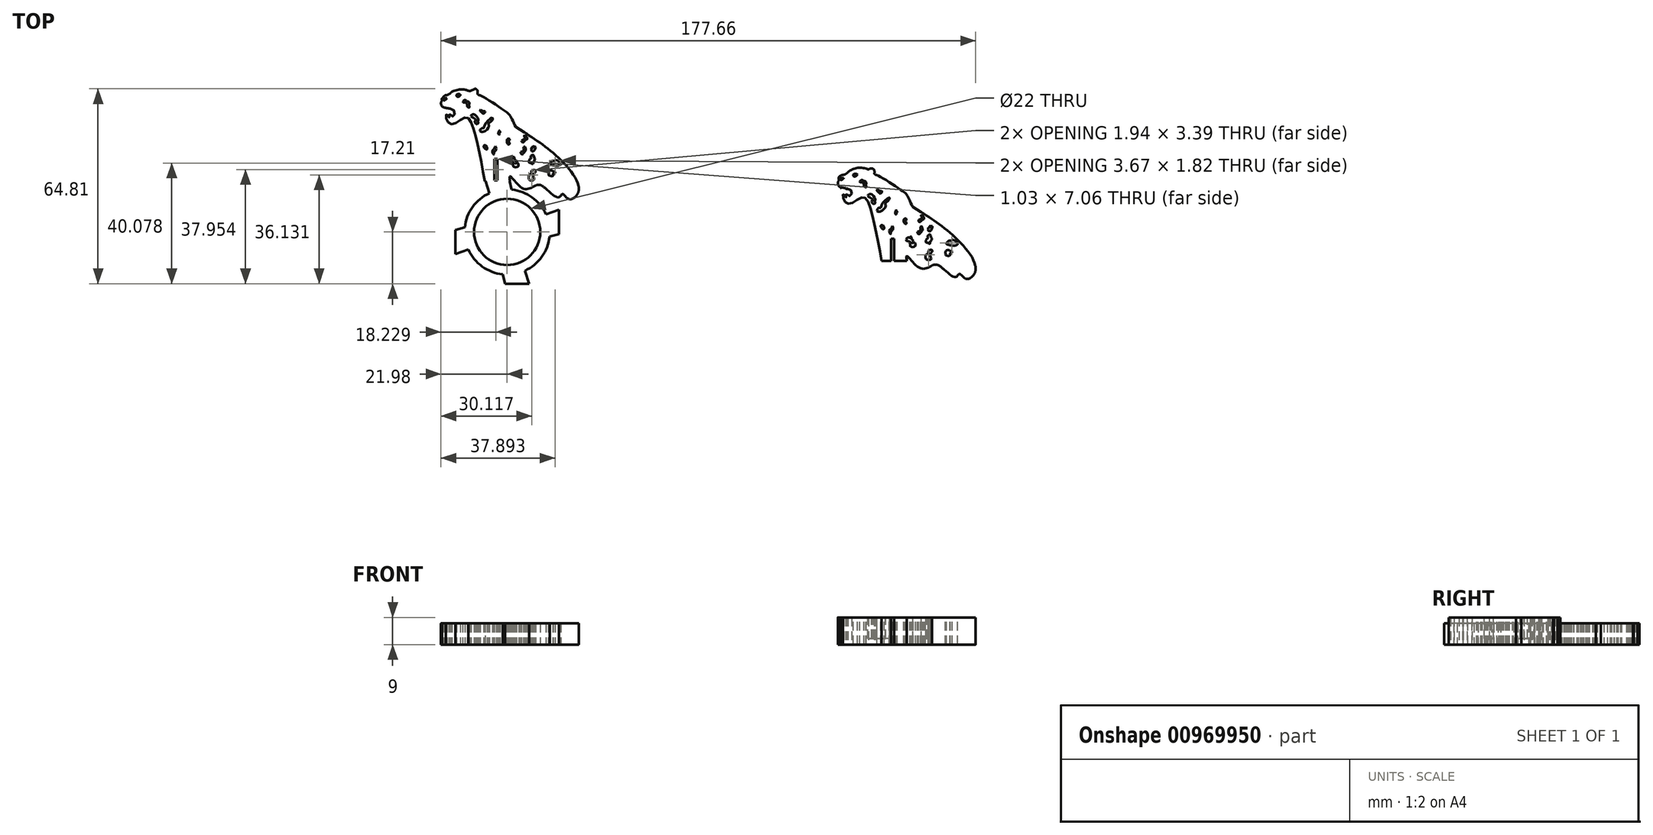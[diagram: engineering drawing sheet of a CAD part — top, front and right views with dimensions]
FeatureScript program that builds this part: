
annotation { "Feature Type Name" : "Feature", "Feature Type Description" : "" }
export const myFeature = defineFeature(function(context is Context, id is Id, definition is map)
    precondition{}
    {
        {
            var Q0;
            Q0=qCreatedBy(makeId("Top.planeOp"),FACE);
            var sketch = newSketch(context, id + "F0", { "sketchPlane" : qUnion([Q0])});
            skCircle(sketch, "E0", {"center": v(0, 0) * mm, "radius": 11 * mm});
            skCircle(sketch, "E1", {"center": v(0, 0) * mm, "radius": 46.71 * mm});
            skArc(sketch, "E2", {"start": v(-5.89, 12.9) * mm, "mid": v(2.27, -14) * mm, "end": v(1.52, 14.1) * mm});
            skLineSegment(sketch, "E3", {"start": v(137.48, 6.65) * mm, "end": v(134.7, 8.38) * mm});
            skFitSpline(sketch, "E4", {"points": [v(134.7, 8.38) * mm, v(132.83, 12.2) * mm, v(131.06, 13.79) * mm, v(122.58, 19) * mm, v(122.4, 19) * mm, v(121.92, 21.06) * mm, v(119.69, 20.4) * mm, v(117.45, 20.87) * mm, v(110.56, 18.26) * mm, v(110.28, 15.18) * mm, v(114.28, 13.79) * mm, v(113.82, 11.92) * mm, v(112.6, 12.67) * mm, v(112.6, 11.55) * mm, v(111.77, 12.58) * mm, v(111.77, 10.8) * mm, v(114, 9.4) * mm, v(118.2, 11.55) * mm, v(121.09, 6.52) * mm, v(124.44, -9.6) * mm], "startDerivative": vector(-33.74, 75.54) * mm, "endDerivative": vector(26.94, -147.55) * mm});
            skLineSegment(sketch, "E5", {"start": v(124.44, -9.6) * mm, "end": v(127.6, -9.6) * mm});
            skLineSegment(sketch, "E6", {"start": v(127.6, -9.6) * mm, "end": v(127.6, -2.24) * mm});
            skLineSegment(sketch, "E7", {"start": v(127.6, -2.24) * mm, "end": v(128.63, -2.24) * mm});
            skLineSegment(sketch, "E8", {"start": v(128.63, -2.24) * mm, "end": v(128.63, -9.6) * mm});
            skLineSegment(sketch, "E9", {"start": v(128.63, -9.6) * mm, "end": v(132.83, -9.6) * mm});
            skFitSpline(sketch, "E10", {"points": [v(132.83, -9.6) * mm, v(132.83, -8.02) * mm, v(136.93, -11.93) * mm, v(141.22, -11.13) * mm], "startDerivative": vector(-1.77, 10.95) * mm, "endDerivative": vector(11.78, 6.45) * mm});
            skFitSpline(sketch, "E11", {"points": [v(141.22, -11.13) * mm, v(143.33, -11.13) * mm, v(148.92, -15.03) * mm, v(150.32, -13.91) * mm, v(152.37, -15.59) * mm, v(155.63, -12.8) * mm, v(148.64, -1.6) * mm, v(137.48, 6.65) * mm], "startDerivative": vector(20.39, 8.24) * mm, "endDerivative": vector(-48.7, 31.34) * mm});
            skFitSpline(sketch, "E12", {"points": [v(155.57, -11.13) * mm, v(162.62, -16.87) * mm], "startDerivative": vector(5.16, -7.62) * mm, "endDerivative": vector(8.98, -3.93) * mm});
            skLineSegment(sketch, "E13", {"start": v(162.62, -16.87) * mm, "end": v(154.78, -14.58) * mm});
            skFitSpline(sketch, "E14", {"points": [v(115.12, 19.2) * mm, v(116.34, 19.1) * mm, v(115.28, 18.46) * mm, v(115.12, 19.2) * mm]});
            skFitSpline(sketch, "E15", {"points": [v(122.82, 7) * mm, v(123.58, 8.07) * mm, v(124.09, 8) * mm, v(124.53, 9.2) * mm, v(126.99, 11.42) * mm, v(126.74, 10.47) * mm, v(125.66, 9.52) * mm, v(125.79, 8.7) * mm, v(124.34, 6.94) * mm, v(122.82, 7) * mm]});
            skFitSpline(sketch, "E16", {"points": [v(124.09, 2.04) * mm, v(124.96, 2.07) * mm, v(125.06, 0.9) * mm, v(124.09, 2.04) * mm]});
            skFitSpline(sketch, "E17", {"points": [v(119.85, 12.04) * mm, v(121.09, 11.13) * mm, v(121.46, 10.56) * mm, v(121.09, 10.24) * mm, v(121.71, 9.3) * mm, v(122.03, 9.55) * mm, v(122.34, 9.67) * mm, v(122.03, 10.43) * mm, v(122.31, 10.46) * mm, v(121.52, 12.17) * mm, v(120.39, 12.58) * mm, v(119.85, 12.04) * mm]});
            skFitSpline(sketch, "E18", {"points": [v(118.2, 16.4) * mm, v(117.64, 16.52) * mm, v(117.13, 16.68) * mm, v(117.96, 17.4) * mm, v(118.4, 16.8) * mm, v(118.84, 16.93) * mm, v(119.34, 15.99) * mm, v(119.15, 15.77) * mm, v(119.28, 15.35) * mm, v(119.28, 14.85) * mm, v(118.65, 15.17) * mm, v(118.55, 15.8) * mm, v(118.2, 16.4) * mm]});
            skFitSpline(sketch, "E19", {"points": [v(128.9, 6.1) * mm, v(128.97, 6.52) * mm, v(129.22, 7.21) * mm, v(129.44, 7.02) * mm, v(129.54, 6.52) * mm, v(129.25, 6.52) * mm, v(129.32, 5.92) * mm, v(128.9, 6.1) * mm]});
            skFitSpline(sketch, "E20", {"points": [v(132.28, 2.64) * mm, v(131.84, 3.27) * mm, v(131.87, 4.18) * mm, v(132.54, 4.47) * mm, v(132.66, 3.96) * mm, v(132.25, 3.74) * mm, v(132.22, 3.36) * mm, v(132.6, 3.2) * mm, v(132.6, 2.73) * mm, v(132.28, 2.64) * mm]});
            skFitSpline(sketch, "E21", {"points": [v(139.04, -8.52) * mm, v(139.23, -7.59) * mm, v(139.98, -7.06) * mm, v(139.9, -6.38) * mm, v(140.92, -5.9) * mm, v(141.3, -6.42) * mm, v(140.5, -7.4) * mm, v(140.73, -8.3) * mm, v(140.77, -9.16) * mm, v(139.87, -9.31) * mm, v(139.23, -9.16) * mm, v(139.04, -8.52) * mm]});
            skFitSpline(sketch, "E22", {"points": [v(141.25, 1.87) * mm, v(140.9, 1.87) * mm, v(140.59, 1.95) * mm, v(140.3, 1.85) * mm, v(140.4, 1.45) * mm, v(139.84, 1.37) * mm, v(139.98, 0.94) * mm, v(139.84, 0.63) * mm, v(140.24, 0.28) * mm, v(140.64, 0.36) * mm, v(141.1, 1) * mm, v(141.25, 1.87) * mm]});
            skFitSpline(sketch, "E23", {"points": [v(132.57, -2.43) * mm, v(133.05, -3.06) * mm, v(133.83, -3.14) * mm, v(133.9, -3.46) * mm, v(133.78, -3.7) * mm, v(133.85, -4.22) * mm, v(133.9, -4.72) * mm, v(134.28, -4.9) * mm, v(134.53, -5.05) * mm, v(134.86, -4.92) * mm, v(135.44, -4.87) * mm, v(135.69, -4.42) * mm, v(135.49, -3.64) * mm, v(135.23, -3.39) * mm, v(134.88, -3.82) * mm, v(134.5, -3.54) * mm, v(134.93, -3.01) * mm, v(134.36, -2.36) * mm, v(134.23, -1.53) * mm, v(133.95, -1.56) * mm, v(133.83, -2.03) * mm, v(133.5, -1.78) * mm, v(132.95, -2.06) * mm, v(132.57, -2.43) * mm]});
            skFitSpline(sketch, "E24", {"points": [v(136.67, 3.8) * mm, v(137.04, 3.27) * mm, v(137.32, 3.4) * mm, v(137.4, 3.67) * mm, v(137.67, 3.67) * mm, v(137.75, 4.2) * mm, v(138.35, 4.2) * mm, v(138.47, 4.87) * mm, v(137.72, 5.48) * mm, v(137.42, 5.37) * mm, v(137.85, 5.02) * mm, v(137.8, 4.55) * mm, v(137.3, 4.2) * mm, v(136.67, 3.8) * mm]});
            skFitSpline(sketch, "E25", {"points": [v(136.31, 0) * mm, v(136.67, -0.68) * mm, v(137.14, -0.58) * mm, v(137.24, -0.3) * mm, v(137.5, -0.25) * mm, v(137.57, 0) * mm, v(138.07, 0.73) * mm, v(137.92, 1.26) * mm, v(137.67, 1.87) * mm, v(137.32, 1.45) * mm, v(137.37, 1) * mm, v(137.1, 0.35) * mm, v(136.31, 0) * mm]});
            skFitSpline(sketch, "E26", {"points": [v(127.98, 1.95) * mm, v(127.53, 1) * mm, v(126.97, 0.5) * mm, v(127.35, -0.73) * mm, v(127.53, 0) * mm, v(127.88, 0.43) * mm, v(128.2, 1) * mm, v(127.98, 1.95) * mm]});
            skFitSpline(sketch, "E27", {"points": [v(146.83, -6.06) * mm, v(147.12, -6.36) * mm, v(147.62, -6.41) * mm, v(147.86, -6.78) * mm, v(147.22, -7.05) * mm, v(147.07, -7.24) * mm, v(147.22, -7.62) * mm, v(146.8, -8) * mm, v(146.08, -7.86) * mm, v(145.61, -7.54) * mm, v(145.68, -7.25) * mm, v(145.56, -6.8) * mm, v(145.75, -6.34) * mm, v(146.12, -6.08) * mm, v(146.83, -6.06) * mm]});
            skFitSpline(sketch, "E28", {"points": [v(147.4, -2.85) * mm, v(146.69, -2.93) * mm, v(146.4, -3.29) * mm, v(145.94, -3.84) * mm, v(146.53, -4.27) * mm, v(147.45, -4.44) * mm, v(148.53, -4.57) * mm, v(149.21, -4.38) * mm, v(149.68, -4.1) * mm, v(149.44, -3.47) * mm, v(148.21, -2.64) * mm, v(147.4, -2.85) * mm]});
            skFitSpline(sketch, "E29", {"points": [v(140.12, -3.88) * mm, v(140.4, -3.92) * mm, v(140.59, -3.5) * mm, v(140.4, -3.34) * mm, v(140.7, -3.2) * mm, v(140.9, -2.87) * mm, v(141.1, -2.14) * mm, v(140.9, -1.86) * mm, v(140.77, -1.46) * mm, v(140.59, -0.92) * mm, v(140.06, -0.93) * mm, v(139.7, -1.67) * mm, v(139.83, -2.06) * mm, v(139.48, -2.26) * mm, v(139.14, -2.9) * mm, v(139.13, -3.44) * mm, v(139.47, -3.52) * mm, v(139.77, -3.64) * mm, v(140.12, -3.88) * mm]});
            skFitSpline(sketch, "E30", {"points": [v(123.2, 14.07) * mm, v(123.7, 13.63) * mm, v(124.33, 13.63) * mm, v(124.6, 13.37) * mm, v(124.3, 13.1) * mm, v(124.01, 12.76) * mm, v(123.44, 13.22) * mm, v(123.06, 13.52) * mm, v(122.87, 13.96) * mm, v(123.2, 14.07) * mm]});
            skLineSegment(sketch, "E31", {"start": v(0, 30.7) * mm, "end": v(131.87, 4.18) * mm, "construction": true});
            skLineSegment(sketch, "E32", {"start": v(-5.89, 12.9) * mm, "end": v(-7.34, 17.21) * mm});
            skLineSegment(sketch, "E33", {"start": v(-7.34, 17.21) * mm, "end": v(0.7, 17.21) * mm});
            skLineSegment(sketch, "E34", {"start": v(0.7, 17.21) * mm, "end": v(1.52, 14.1) * mm});
            skArc(sketch, "E35", {"start": v(110.28, 17.32) * mm, "mid": v(109.9, 16.25) * mm, "end": v(110.28, 15.18) * mm});
            skFitSpline(sketch, "E36.trimOffspring", {"points": [v(134.7, 8.38) * mm, v(132.83, 12.2) * mm, v(131.06, 13.79) * mm, v(122.58, 19) * mm, v(122.4, 19) * mm, v(121.92, 21.06) * mm, v(119.69, 20.4) * mm, v(117.45, 20.87) * mm, v(110.56, 18.26) * mm, v(110.28, 15.18) * mm, v(114.28, 13.79) * mm, v(113.82, 11.92) * mm, v(112.6, 12.67) * mm, v(112.6, 11.55) * mm, v(111.77, 12.58) * mm, v(111.77, 10.8) * mm, v(114, 9.4) * mm, v(118.2, 11.55) * mm, v(121.09, 6.52) * mm, v(124.44, -9.6) * mm], "startDerivative": vector(-33.74, 75.54) * mm, "endDerivative": vector(26.94, -147.55) * mm});
            skArc(sketch, "E37", {"start": v(110.16, 18.1) * mm, "mid": v(110.12, 17.7) * mm, "end": v(110.28, 17.32) * mm});
            skArc(sketch, "E38", {"start": v(111.62, 18.97) * mm, "mid": v(110.79, 18.7) * mm, "end": v(110.16, 18.1) * mm});
            skArc(sketch, "E39", {"start": v(111.62, 18.97) * mm, "mid": v(112.5, 19.26) * mm, "end": v(113.18, 19.88) * mm});
            skArc(sketch, "E40", {"start": v(120.05, 20.73) * mm, "mid": v(116.5, 21.31) * mm, "end": v(113.18, 19.88) * mm});
            skArc(sketch, "E41", {"start": v(122.03, 20.5) * mm, "mid": v(121.1, 21.12) * mm, "end": v(120.05, 20.73) * mm});
            skArc(sketch, "E42", {"start": v(122.03, 19.27) * mm, "mid": v(122.05, 19.88) * mm, "end": v(122.03, 20.5) * mm});
            skArc(sketch, "E43", {"start": v(122.4, 19) * mm, "mid": v(122.23, 19.17) * mm, "end": v(122.03, 19.27) * mm});
            skPoint(sketch, "E44.2.internal.orphan", {"position": v(110.56, 16.86) * mm});
            skArc(sketch, "E45", {"start": v(111.14, 17.89) * mm, "mid": v(110.75, 17.9) * mm, "end": v(110.72, 17.5) * mm});
            skArc(sketch, "E46", {"start": v(111.14, 17.89) * mm, "mid": v(111.5, 17.92) * mm, "end": v(111.87, 17.96) * mm});
            skArc(sketch, "E47", {"start": v(111.06, 17.26) * mm, "mid": v(111.52, 17.55) * mm, "end": v(111.87, 17.96) * mm});
            skArc(sketch, "E48", {"start": v(110.72, 17.5) * mm, "mid": v(110.82, 17.29) * mm, "end": v(111.06, 17.26) * mm});
            skArc(sketch, "E49", {"start": v(139.78, -11.91) * mm, "mid": v(139.1, -12.6) * mm, "end": v(139.36, -13.56) * mm});
            skArc(sketch, "E50", {"start": v(139.36, -13.56) * mm, "mid": v(139.6, -13.92) * mm, "end": v(140.05, -13.93) * mm});
            skArc(sketch, "E51", {"start": v(142.33, -12.8) * mm, "mid": v(141.14, -13.27) * mm, "end": v(140.05, -13.93) * mm});
            skArc(sketch, "E52", {"start": v(145.2, -12.55) * mm, "mid": v(143.74, -12.43) * mm, "end": v(142.33, -12.8) * mm});
            skLineSegment(sketch, "E53", {"start": v(139.78, -11.91) * mm, "end": v(141.22, -11.13) * mm});
            skArc(sketch, "E54", {"start": v(110.65, 14.56) * mm, "mid": v(110.69, 14.77) * mm, "end": v(110.67, 14.97) * mm});
            skArc(sketch, "E55", {"start": v(110.65, 14.56) * mm, "mid": v(110.88, 14.65) * mm, "end": v(111.03, 14.85) * mm});
            skArc(sketch, "E56", {"start": v(112.88, 14.15) * mm, "mid": v(112.93, 14.32) * mm, "end": v(112.87, 14.49) * mm});
            skArc(sketch, "E57", {"start": v(112.48, 14.56) * mm, "mid": v(112.64, 14.31) * mm, "end": v(112.88, 14.15) * mm});
            skSolve(sketch);
        }
        {
            var Q0;
            {var subQ5=sQuery(id+"F0.wireOp",EDGE,"E3");Q0=makeQuery(id+"F0.imprint","IMPRINT",FACE,{"disambiguationData":[TD([[makeQuery(id+"F0.imprint","IMPRINT",EDGE,{"derivedFrom":subQ5}),1.0]])]});}
            extrude(context, id + "F1", {"entities" : qUnion([Q0]), "depth" : 7 * mm, "offsetDistance" : 25 * mm});
        }
        {
            var Q0;
            Q0=qCreatedBy(makeId("Top.planeOp"),FACE);
            var sketch = newSketch(context, id + "F2", { "sketchPlane" : qUnion([Q0])});
            skCircle(sketch, "E58", {"center": v(0, 0) * mm, "radius": 11 * mm});
            skSolve(sketch);
        }
        {
            var Q0;
            Q0=makeQuery(id+"F1.opExtrude","SWEPT_BODY",BODY,{"disambiguationData":[OSD([sQuery(id+"F0.wireOp",EDGE,"E3"),sQuery(id+"F0.wireOp",EDGE,"E4"),sQuery(id+"F0.wireOp",EDGE,"E5"),sQuery(id+"F0.wireOp",EDGE,"E6"),sQuery(id+"F0.wireOp",EDGE,"E7"),sQuery(id+"F0.wireOp",EDGE,"E8"),sQuery(id+"F0.wireOp",EDGE,"E9"),sQuery(id+"F0.wireOp",EDGE,"E10"),sQuery(id+"F0.wireOp",EDGE,"E11"),sQuery(id+"F0.wireOp",EDGE,"E12"),sQuery(id+"F0.wireOp",EDGE,"E13"),sQuery(id+"F0.wireOp",EDGE,"E11"),sQuery(id+"F0.wireOp",EDGE,"E14"),sQuery(id+"F0.wireOp",EDGE,"E44"),sQuery(id+"F0.wireOp",EDGE,"E15"),sQuery(id+"F0.wireOp",EDGE,"E16"),sQuery(id+"F0.wireOp",EDGE,"E17"),sQuery(id+"F0.wireOp",EDGE,"E18"),sQuery(id+"F0.wireOp",EDGE,"E19"),sQuery(id+"F0.wireOp",EDGE,"E20"),sQuery(id+"F0.wireOp",EDGE,"E21"),sQuery(id+"F0.wireOp",EDGE,"E22"),sQuery(id+"F0.wireOp",EDGE,"E23"),sQuery(id+"F0.wireOp",EDGE,"E24"),sQuery(id+"F0.wireOp",EDGE,"E25"),sQuery(id+"F0.wireOp",EDGE,"E26"),sQuery(id+"F0.wireOp",EDGE,"E27"),sQuery(id+"F0.wireOp",EDGE,"E28"),sQuery(id+"F0.wireOp",EDGE,"E29"),sQuery(id+"F0.wireOp",EDGE,"E30")])]});
            var Q1;
            Q1=sQuery(id+"F0.wireOp",VERTEX,"E20.2.internal");
            var Q2;
            Q2=sQuery(id+"F0.wireOp",VERTEX,"E31.start");
            transform(context, id + "F3", {"entities" : qUnion([Q0]), "transformType" : TransformType.TRANSLATION_ENTITY, "oppositeDirectionEntity" : false, "transformLine" : qUnion([Q1, Q2]), "makeCopy" : false});
        }
        {
            var Q0;
            Q0=makeQuery(id+"F0.imprint","IMPRINT",FACE,{"disambiguationData":[TD([[makeQuery(id+"F0.imprint","IMPRINT",EDGE,{"derivedFrom":sQuery(id+"F0.wireOp",EDGE,"E0")}),-1.0]])]});
            var Q1;
            {var subQ0=sQuery(id+"F0.wireOp",EDGE,"E44");var subQ1=sQuery(id+"F0.wireOp",EDGE,"E4");var subQ2=makeQuery(id+"F0.imprint","INTERSECT",VERTEX,{"disambiguationData":[OD(0.0)],"derivedFrom":[subQ1,subQ0]});Q1=makeQuery(id+"F0.imprint","IMPRINT",FACE,{"disambiguationData":[TD([[makeQuery(id+"F0.imprint","IMPRINT",EDGE,{"disambiguationData":[TD([[subQ2,-1.0]])],"derivedFrom":subQ1}),-1.0]])]});}
            var Q2;
            {var subQ0=sQuery(id+"F0.wireOp",EDGE,"E44");var subQ1=sQuery(id+"F0.wireOp",EDGE,"E4");var subQ2=makeQuery(id+"F0.imprint","INTERSECT",VERTEX,{"disambiguationData":[OD(0.0)],"derivedFrom":[subQ1,subQ0]});Q2=makeQuery(id+"F0.imprint","IMPRINT",FACE,{"disambiguationData":[TD([[makeQuery(id+"F0.imprint","IMPRINT",EDGE,{"disambiguationData":[TD([[subQ2,-1.0]])],"derivedFrom":subQ1}),1.0]])]});}
            var Q3;
            {var subQ5=sQuery(id+"F0.wireOp",EDGE,"E3");Q3=makeQuery(id+"F0.imprint","IMPRINT",FACE,{"disambiguationData":[TD([[makeQuery(id+"F0.imprint","IMPRINT",EDGE,{"derivedFrom":subQ5}),1.0]])]});}
            extrude(context, id + "F4", {"entities" : qUnion([Q0, Q1, Q2, Q3]), "depth" : 7 * mm, "offsetDistance" : 25 * mm});
        }
        {
            var Q0;
            Q0=makeQuery(id+"F4.opExtrude","CAP_FACE",FACE,{"disambiguationData":[OSD([sQuery(id+"F0.wireOp",EDGE,"E3"),sQuery(id+"F0.wireOp",EDGE,"E4"),sQuery(id+"F0.wireOp",EDGE,"E5"),sQuery(id+"F0.wireOp",EDGE,"E6"),sQuery(id+"F0.wireOp",EDGE,"E7"),sQuery(id+"F0.wireOp",EDGE,"E8"),sQuery(id+"F0.wireOp",EDGE,"E9"),sQuery(id+"F0.wireOp",EDGE,"E10"),sQuery(id+"F0.wireOp",EDGE,"E11"),sQuery(id+"F0.wireOp",EDGE,"E12"),sQuery(id+"F0.wireOp",EDGE,"E13"),sQuery(id+"F0.wireOp",EDGE,"E11"),sQuery(id+"F0.wireOp",EDGE,"E14"),sQuery(id+"F0.wireOp",EDGE,"E44"),sQuery(id+"F0.wireOp",EDGE,"E15"),sQuery(id+"F0.wireOp",EDGE,"E16"),sQuery(id+"F0.wireOp",EDGE,"E17"),sQuery(id+"F0.wireOp",EDGE,"E18"),sQuery(id+"F0.wireOp",EDGE,"E19"),sQuery(id+"F0.wireOp",EDGE,"E20"),sQuery(id+"F0.wireOp",EDGE,"E21"),sQuery(id+"F0.wireOp",EDGE,"E22"),sQuery(id+"F0.wireOp",EDGE,"E23"),sQuery(id+"F0.wireOp",EDGE,"E24"),sQuery(id+"F0.wireOp",EDGE,"E25"),sQuery(id+"F0.wireOp",EDGE,"E26"),sQuery(id+"F0.wireOp",EDGE,"E27"),sQuery(id+"F0.wireOp",EDGE,"E28"),sQuery(id+"F0.wireOp",EDGE,"E29"),sQuery(id+"F0.wireOp",EDGE,"E30")])],"isStart":false});
            var Q1;
            Q1=makeQuery(id+"F0.imprint","IMPRINT",FACE,{"disambiguationData":[TD([[makeQuery(id+"F0.imprint","IMPRINT",EDGE,{"derivedFrom":sQuery(id+"F0.wireOp",EDGE,"E15")}),-1.0]])]});
            var Q2;
            Q2=makeQuery(id+"F0.imprint","IMPRINT",FACE,{"disambiguationData":[TD([[makeQuery(id+"F0.imprint","IMPRINT",EDGE,{"derivedFrom":sQuery(id+"F0.wireOp",EDGE,"E17")}),1.0]])]});
            var Q3;
            Q3=makeQuery(id+"F0.imprint","IMPRINT",FACE,{"disambiguationData":[TD([[makeQuery(id+"F0.imprint","IMPRINT",EDGE,{"derivedFrom":sQuery(id+"F0.wireOp",EDGE,"E29")}),1.0]])]});
            extrude(context, id + "F5", {"entities" : qUnion([Q0, Q1, Q2, Q3]), "operationType" : NewBodyOperationType.ADD, "depth" : 2 * mm, "offsetDistance" : 25 * mm});
        }
        {
            var Q0;
            Q0=makeQuery(id+"F4.opExtrude","SWEPT_BODY",BODY,{"disambiguationData":[OSD([sQuery(id+"F0.wireOp",EDGE,"E0"),sQuery(id+"F0.wireOp",EDGE,"E2"),sQuery(id+"F0.wireOp",EDGE,"E32"),sQuery(id+"F0.wireOp",EDGE,"E33"),sQuery(id+"F0.wireOp",EDGE,"E34")])]});
            var Q1;
            Q1=sQuery(id+"F2.wireOp",EDGE,"E58");
            circularPattern(context, id + "F6", {"operationType" : NewBodyOperationType.ADD, "entities" : qUnion([Q0]), "axis" : qUnion([Q1]), "angle" : 360 * degree, "instanceCount" : 4, "equalSpace" : true});
        }
    });
